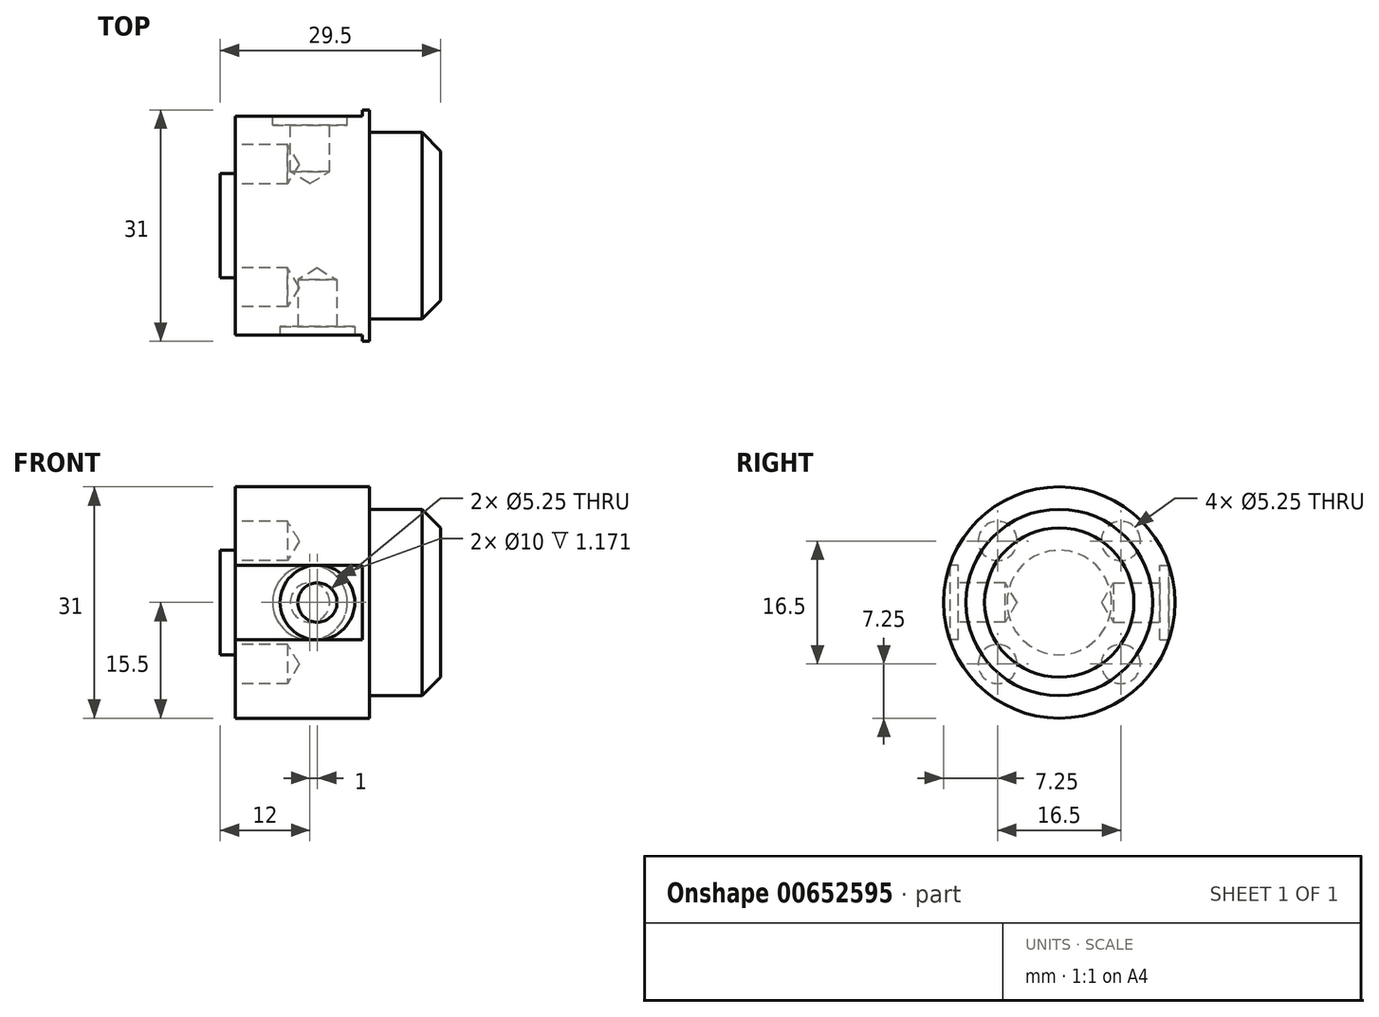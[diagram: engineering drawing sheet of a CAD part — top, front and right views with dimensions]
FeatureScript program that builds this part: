
annotation { "Feature Type Name" : "Feature", "Feature Type Description" : "" }
export const myFeature = defineFeature(function(context is Context, id is Id, definition is map)
    precondition{}
    {
        {
            var Q0;
            Q0=qCreatedBy(makeId("Front.planeOp"),FACE);
            var sketch = newSketch(context, id + "F0", { "sketchPlane" : qUnion([Q0])});
            skLineSegment(sketch, "E0", {"start": v(0, 5) * mm, "end": v(0, 15.5) * mm});
            skLineSegment(sketch, "E1", {"start": v(0, 15.5) * mm, "end": v(-18, 15.5) * mm});
            skLineSegment(sketch, "E2", {"start": v(-18, 15.5) * mm, "end": v(-18, 7) * mm});
            skLineSegment(sketch, "E3", {"start": v(-18, 7) * mm, "end": v(-20, 7) * mm});
            skLineSegment(sketch, "E4", {"start": v(-20, 7) * mm, "end": v(-20, 5) * mm});
            skPoint(sketch, "E5.startSnap0", {"position": v(0, 7.75) * mm});
            skPoint(sketch, "E6.end.orphan", {"position": v(0, 0) * mm});
            skPoint(sketch, "E7.orphan", {"position": v(-20, 0) * mm});
            skLineSegment(sketch, "E8", {"start": v(0, 0) * mm, "end": v(-10.6, 0) * mm, "construction": true});
            skLineSegment(sketch, "E9", {"start": v(-20, 5) * mm, "end": v(-20, 0) * mm});
            skLineSegment(sketch, "E10", {"start": v(0, 5) * mm, "end": v(0, 0) * mm});
            skLineSegment(sketch, "E11", {"start": v(-20, 0) * mm, "end": v(0, 0) * mm});
            skSolve(sketch);
        }
        {
            var Q0;
            Q0 = qSketchRegion(id + "F0", true);
            var Q1;
            Q1=sQuery(id+"F0.wireOp",EDGE,"E8");
            revolve(context, id + "F1", {"entities" : qUnion([Q0]), "axis" : qUnion([Q1]), "revolveType" : RevolveType.FULL});
        }
        {
            var Q0;
            Q0=makeQuery(id+"F1.opRevolve","SWEPT_FACE",FACE,{"disambiguationData":[OSD([sQuery(id+"F0.wireOp",EDGE,"E2")])]});
            var sketch = newSketch(context, id + "F2", { "sketchPlane" : qUnion([Q0])});
            skCircle(sketch, "E12", {"center": v(8.25, 8.25) * mm, "radius": 1.5 * mm});
            skCircle(sketch, "E13.1.0", {"center": v(-8.25, 8.25) * mm, "radius": 1.5 * mm});
            skCircle(sketch, "E13.2.0", {"center": v(-8.25, -8.25) * mm, "radius": 1.5 * mm});
            skCircle(sketch, "E13.3.0", {"center": v(8.25, -8.25) * mm, "radius": 1.5 * mm});
            skPoint(sketch, "E13.center", {"position": v(0, 0) * mm});
            skSolve(sketch);
        }
        {
            var Q0;
            Q0 = qSketchRegion(id + "F2", true);
            extrude(context, id + "F3", {"entities" : qUnion([Q0]), "operationType" : NewBodyOperationType.REMOVE, "oppositeDirection" : true, "depth" : 5 * mm, "offsetDistance" : 25 * mm});
        }
        {
            var Q0;
            Q0=makeQuery(id+"F1.opRevolve","SWEPT_FACE",FACE,{"disambiguationData":[OSD([sQuery(id+"F0.wireOp",EDGE,"E2")])]});
            var sketch = newSketch(context, id + "F4", { "sketchPlane" : qUnion([Q0])});
            skCircle(sketch, "E14", {"center": v(-8.25, 8.25) * mm, "radius": 0.94 * mm});
            skCircle(sketch, "E15.1.0", {"center": v(-8.25, -8.25) * mm, "radius": 0.94 * mm});
            skCircle(sketch, "E15.2.0", {"center": v(8.25, -8.25) * mm, "radius": 0.94 * mm});
            skCircle(sketch, "E15.3.0", {"center": v(8.25, 8.25) * mm, "radius": 0.94 * mm});
            skPoint(sketch, "E15.center", {"position": v(0, 0) * mm});
            skSolve(sketch);
        }
        {
            var Q0;
            Q0=sQuery(id+"F4.wireOp",VERTEX,"E14.center");
            var Q1;
            Q1=sQuery(id+"F4.wireOp",VERTEX,"E15.3.0.center");
            var Q2;
            Q2=sQuery(id+"F4.wireOp",VERTEX,"E15.1.0.center");
            var Q3;
            Q3=sQuery(id+"F4.wireOp",VERTEX,"E15.2.0.center");
            var Q4;
            Q4=makeQuery(id+"F1.opRevolve","SWEPT_BODY",BODY,{"disambiguationData":[OSD([sQuery(id+"F0.wireOp",EDGE,"E0"),sQuery(id+"F0.wireOp",EDGE,"E1"),sQuery(id+"F0.wireOp",EDGE,"E2"),sQuery(id+"F0.wireOp",EDGE,"E3"),sQuery(id+"F0.wireOp",EDGE,"E4"),sQuery(id+"F0.wireOp",EDGE,"E9"),sQuery(id+"F0.wireOp",EDGE,"E10"),sQuery(id+"F0.wireOp",EDGE,"E11")])]});
            hole(context, id + "F5", {"style" : HoleStyle.SIMPLE, "endStyle" : HoleEndStyle.BLIND, "standardTappedOrClearance" : lookupTablePath({ "standard" : "ISO", "engagement" : "75%", "pitch" : "0.75 mm", "size" : "M6", "type" : "Tapped" }), "standardBlindInLast" : lookupTablePath({ "standard" : "ISO", "engagement" : "75%", "pitch" : "0.75 mm", "size" : "M6", "type" : "Tapped" }), "holeDiameter" : 5.25 * mm, "majorDiameter" : 6 * mm, "showTappedDepth" : true, "holeDepth" : 7 * mm, "isTappedThrough" : true, "tappedDepth" : 6.25 * mm, "tapClearance" : 1, "locations" : qUnion([Q0, Q1, Q2, Q3]), "scope" : qUnion([Q4])});
        }
        {
            var Q0;
            Q0=qCreatedBy(makeId("Front.planeOp"),FACE);
            cPlane(context, id + "F6", {"entities" : qUnion([Q0]), "cplaneType" : CPlaneType.OFFSET, "offset" : 15.5 * mm, "width" : 150 * mm, "height" : 150 * mm});
        }
        {
            var Q0;
            Q0=qCreatedBy(id+"F6.planeOp",FACE);
            var sketch = newSketch(context, id + "F7", { "sketchPlane" : qUnion([Q0])});
            skCircle(sketch, "E16", {"center": v(-7, 0) * mm, "radius": 5 * mm});
            skSolve(sketch);
        }
        {
            var Q0;
            Q0 = qSketchRegion(id + "F7", true);
            extrude(context, id + "F8", {"entities" : qUnion([Q0]), "operationType" : NewBodyOperationType.REMOVE, "oppositeDirection" : true, "depth" : 2 * mm, "offsetDistance" : 25 * mm});
        }
        {
            var Q0;
            Q0=makeQuery(id+"F8.boolean.opBoolean","COPY",FACE,{"derivedFrom":makeQuery(id+"F8.opExtrude","CAP_FACE",FACE,{"disambiguationData":[OSD([sQuery(id+"F7.wireOp",EDGE,"E16")])],"isStart":false})});
            var sketch = newSketch(context, id + "F9", { "sketchPlane" : qUnion([Q0])});
            skCircle(sketch, "E17", {"center": v(-7, 0) * mm, "radius": 2.73 * mm});
            skSolve(sketch);
        }
        {
            var Q0;
            Q0=sQuery(id+"F9.wireOp",VERTEX,"E17.center");
            var Q1;
            Q1=makeQuery(id+"F1.opRevolve","SWEPT_BODY",BODY,{"disambiguationData":[OSD([sQuery(id+"F0.wireOp",EDGE,"E0"),sQuery(id+"F0.wireOp",EDGE,"E1"),sQuery(id+"F0.wireOp",EDGE,"E2"),sQuery(id+"F0.wireOp",EDGE,"E3"),sQuery(id+"F0.wireOp",EDGE,"E4"),sQuery(id+"F0.wireOp",EDGE,"E9"),sQuery(id+"F0.wireOp",EDGE,"E10"),sQuery(id+"F0.wireOp",EDGE,"E11")])]});
            hole(context, id + "F10", {"style" : HoleStyle.SIMPLE, "endStyle" : HoleEndStyle.BLIND, "standardTappedOrClearance" : lookupTablePath({ "standard" : "ISO", "engagement" : "75%", "pitch" : "0.75 mm", "size" : "M6", "type" : "Tapped" }), "standardBlindInLast" : lookupTablePath({ "standard" : "ISO", "engagement" : "75%", "pitch" : "0.75 mm", "size" : "M6", "type" : "Tapped" }), "holeDiameter" : 5.25 * mm, "majorDiameter" : 6 * mm, "showTappedDepth" : true, "holeDepth" : 6.25 * mm, "isTappedThrough" : true, "tappedDepth" : 6.25 * mm, "tapClearance" : 0, "locations" : qUnion([Q0]), "scope" : qUnion([Q1])});
        }
        {
            var Q0;
            Q0=qCreatedBy(makeId("Front.planeOp"),FACE);
            cPlane(context, id + "F11", {"entities" : qUnion([Q0]), "cplaneType" : CPlaneType.OFFSET, "offset" : 15.5 * mm, "oppositeDirection" : true, "width" : 150 * mm, "height" : 150 * mm});
        }
        {
            var Q0;
            Q0=qCreatedBy(id+"F11.planeOp",FACE);
            var sketch = newSketch(context, id + "F12", { "sketchPlane" : qUnion([Q0])});
            skCircle(sketch, "E18", {"center": v(-8, 0) * mm, "radius": 5 * mm});
            skSolve(sketch);
        }
        {
            var Q0;
            Q0 = qSketchRegion(id + "F12", true);
            extrude(context, id + "F13", {"entities" : qUnion([Q0]), "operationType" : NewBodyOperationType.REMOVE, "depth" : 2 * mm, "offsetDistance" : 25 * mm});
        }
        {
            var Q0;
            Q0=makeQuery(id+"F13.boolean.opBoolean","COPY",FACE,{"derivedFrom":makeQuery(id+"F13.opExtrude","CAP_FACE",FACE,{"disambiguationData":[OSD([sQuery(id+"F12.wireOp",EDGE,"E18")])],"isStart":false})});
            var sketch = newSketch(context, id + "F14", { "sketchPlane" : qUnion([Q0])});
            skCircle(sketch, "E19", {"center": v(8, 0) * mm, "radius": 1.83 * mm});
            skSolve(sketch);
        }
        {
            var Q0;
            Q0=sQuery(id+"F14.wireOp",VERTEX,"E19.center");
            var Q1;
            Q1=makeQuery(id+"F1.opRevolve","SWEPT_BODY",BODY,{"disambiguationData":[OSD([sQuery(id+"F0.wireOp",EDGE,"E0"),sQuery(id+"F0.wireOp",EDGE,"E1"),sQuery(id+"F0.wireOp",EDGE,"E2"),sQuery(id+"F0.wireOp",EDGE,"E3"),sQuery(id+"F0.wireOp",EDGE,"E4"),sQuery(id+"F0.wireOp",EDGE,"E9"),sQuery(id+"F0.wireOp",EDGE,"E10"),sQuery(id+"F0.wireOp",EDGE,"E11")])]});
            hole(context, id + "F15", {"style" : HoleStyle.SIMPLE, "endStyle" : HoleEndStyle.BLIND, "standardTappedOrClearance" : lookupTablePath({ "standard" : "ISO", "engagement" : "75%", "pitch" : "0.75 mm", "size" : "M6", "type" : "Tapped" }), "standardBlindInLast" : lookupTablePath({ "standard" : "ISO", "engagement" : "75%", "pitch" : "0.75 mm", "size" : "M6", "type" : "Tapped" }), "holeDiameter" : 5.25 * mm, "majorDiameter" : 6 * mm, "showTappedDepth" : true, "holeDepth" : 6.25 * mm, "isTappedThrough" : true, "tappedDepth" : 6.25 * mm, "tapClearance" : 0, "locations" : qUnion([Q0]), "scope" : qUnion([Q1])});
        }
        {
            var Q0;
            Q0=makeQuery(id+"F1.opRevolve","SWEPT_FACE",FACE,{"disambiguationData":[OSD([sQuery(id+"F0.wireOp",EDGE,"E0"),sQuery(id+"F0.wireOp",EDGE,"E10")])]});
            var sketch = newSketch(context, id + "F16", { "sketchPlane" : qUnion([Q0])});
            skCircle(sketch, "E20", {"center": v(0, 0) * mm, "radius": 12.5 * mm});
            skSolve(sketch);
        }
        {
            var Q0;
            Q0 = qSketchRegion(id + "F16", true);
            extrude(context, id + "F17", {"entities" : qUnion([Q0]), "operationType" : NewBodyOperationType.ADD, "depth" : 9.5 * mm, "offsetDistance" : 25 * mm});
        }
        {
            var Q0;
            Q0=makeQuery(id+"F17.opExtrude","CAP_EDGE",EDGE,{"disambiguationData":[OSD([sQuery(id+"F16.wireOp",EDGE,"E20")])],"isStart":false});
            chamfer(context, id + "F18", {"entities" : qUnion([Q0]), "width" : 2.5 * mm, "tangentPropagation" : true});
        }
        {
            var Q0;
            Q0=makeQuery(id+"F1.opRevolve","SWEPT_FACE",FACE,{"disambiguationData":[OSD([sQuery(id+"F0.wireOp",EDGE,"E2")])]});
            var sketch = newSketch(context, id + "F19", { "sketchPlane" : qUnion([Q0])});
            skArc(sketch, "E21", {"start": v(-14.67, 5) * mm, "mid": v(-15.5, 0) * mm, "end": v(-14.67, -5) * mm});
            skLineSegment(sketch, "E22", {"start": v(14.67, 5) * mm, "end": v(14.67, -5) * mm});
            skLineSegment(sketch, "E23", {"start": v(-14.67, 5) * mm, "end": v(-14.67, -5) * mm});
            skArc(sketch, "E24.trimOffspring", {"start": v(14.67, -5) * mm, "mid": v(15.5, 0) * mm, "end": v(14.67, 5) * mm});
            skSolve(sketch);
        }
        {
            var Q0;
            Q0 = qSketchRegion(id + "F19", true);
            extrude(context, id + "F20", {"entities" : qUnion([Q0]), "operationType" : NewBodyOperationType.REMOVE, "oppositeDirection" : true, "depth" : 17 * mm, "offsetDistance" : 25 * mm});
        }
    });
